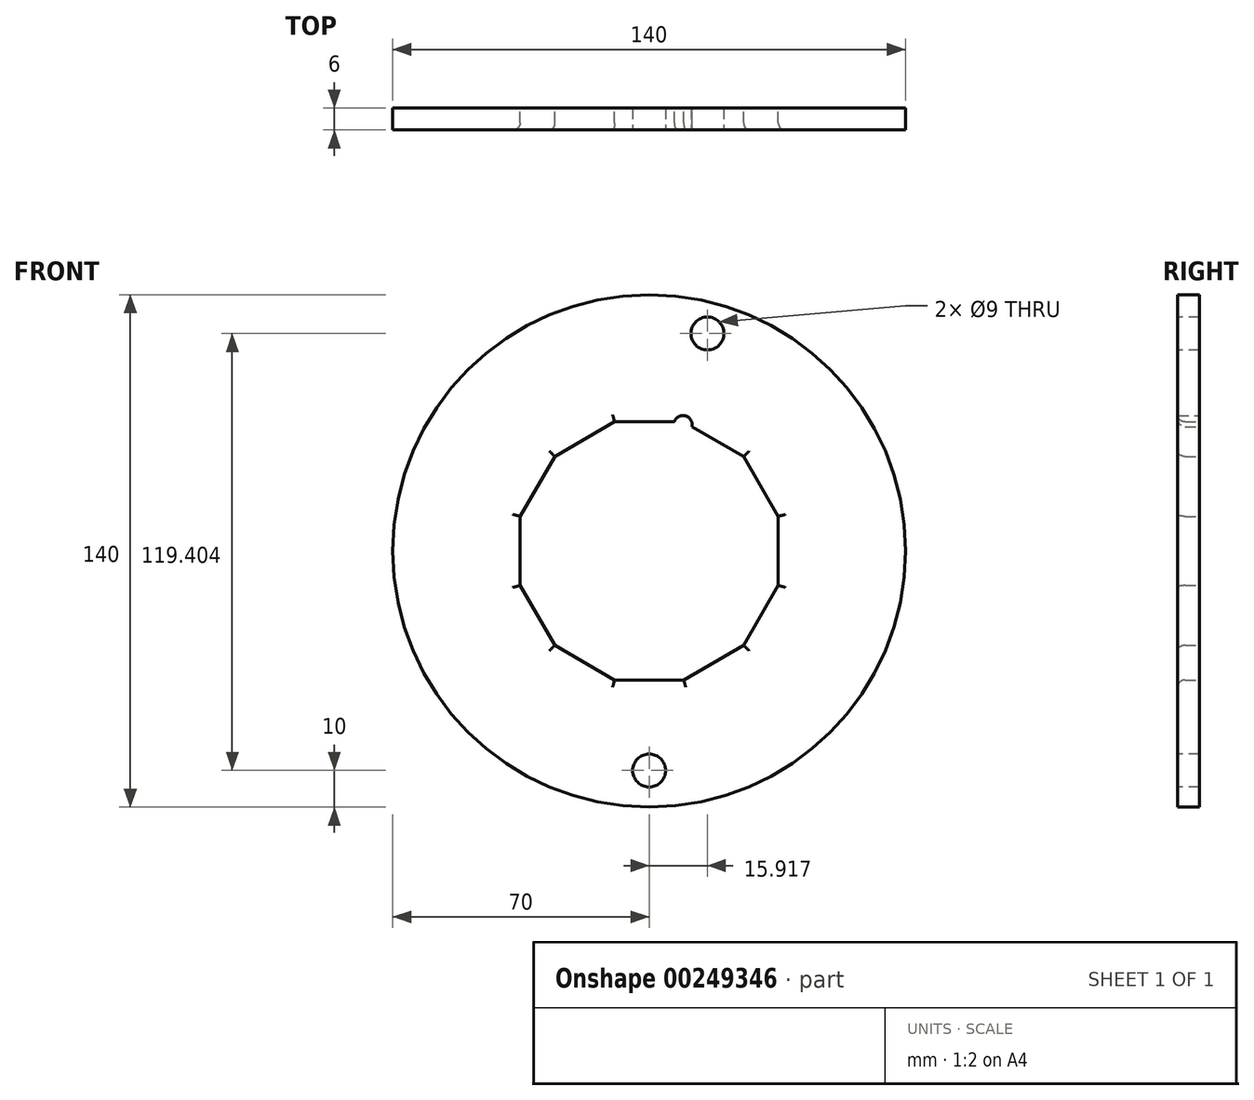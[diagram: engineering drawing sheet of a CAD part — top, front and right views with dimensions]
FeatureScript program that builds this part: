
annotation { "Feature Type Name" : "Feature", "Feature Type Description" : "" }
export const myFeature = defineFeature(function(context is Context, id is Id, definition is map)
    precondition{}
    {
        {
            var Q0;
            Q0=qCreatedBy(makeId("Front.planeOp"),FACE);
            var sketch = newSketch(context, id + "F0", { "sketchPlane" : qUnion([Q0])});
            skCircle(sketch, "E0.cCircle", {"center": v(0, 0) * mm, "radius": 35.25 * mm, "construction": true});
            skLineSegment(sketch, "E0.0", {"start": v(-9.45, 35.25) * mm, "end": v(9.45, 35.25) * mm});
            skLineSegment(sketch, "E0.1", {"start": v(9.45, 35.25) * mm, "end": v(25.8, 25.8) * mm});
            skLineSegment(sketch, "E0.2", {"start": v(25.8, 25.8) * mm, "end": v(35.25, 9.45) * mm});
            skLineSegment(sketch, "E0.3", {"start": v(35.25, 9.45) * mm, "end": v(35.25, -9.45) * mm});
            skLineSegment(sketch, "E0.4", {"start": v(35.25, -9.45) * mm, "end": v(25.8, -25.8) * mm});
            skLineSegment(sketch, "E0.5", {"start": v(25.8, -25.8) * mm, "end": v(9.45, -35.25) * mm});
            skLineSegment(sketch, "E0.6", {"start": v(9.45, -35.25) * mm, "end": v(-9.45, -35.25) * mm});
            skLineSegment(sketch, "E0.7", {"start": v(-9.45, -35.25) * mm, "end": v(-25.8, -25.8) * mm});
            skLineSegment(sketch, "E0.8", {"start": v(-25.8, -25.8) * mm, "end": v(-35.25, -9.45) * mm});
            skLineSegment(sketch, "E0.9", {"start": v(-35.25, -9.45) * mm, "end": v(-35.25, 9.45) * mm});
            skLineSegment(sketch, "E0.10", {"start": v(-35.25, 9.45) * mm, "end": v(-25.8, 25.8) * mm});
            skLineSegment(sketch, "E0.11", {"start": v(-25.8, 25.8) * mm, "end": v(-9.45, 35.25) * mm});
            skPoint(sketch, "E0.0.midPoint", {"position": v(0, 35.25) * mm});
            skCircle(sketch, "E1", {"center": v(0, 0) * mm, "radius": 70 * mm});
            skSolve(sketch);
        }
        {
            var Q0;
            Q0=makeQuery(id+"F0.imprint","IMPRINT",FACE,{"disambiguationData":[TD([[makeQuery(id+"F0.imprint","IMPRINT",EDGE,{"derivedFrom":sQuery(id+"F0.wireOp",EDGE,"E0.0")}),1.0]])]});
            extrude(context, id + "F1", {"entities" : qUnion([Q0]), "depth" : 6 * mm, "symmetric" : true});
        }
        {
            var Q0;
            Q0=qCreatedBy(makeId("Front.planeOp"),FACE);
            var sketch = newSketch(context, id + "F2", { "sketchPlane" : qUnion([Q0])});
            skCircle(sketch, "E2", {"center": v(9.24, 34.48) * mm, "radius": 2.5 * mm});
            skLineSegment(sketch, "E3", {"start": v(9.24, 34.48) * mm, "end": v(0, 0) * mm, "construction": true});
            skSolve(sketch);
        }
        {
            var Q0;
            Q0=makeQuery(id+"F1.opExtrude","CAP_EDGE",EDGE,{"disambiguationData":[OSD([sQuery(id+"F0.wireOp",EDGE,"E0.11")])],"isStart":false});
            var Q1;
            Q1=makeQuery(id+"F1.opExtrude","CAP_EDGE",EDGE,{"disambiguationData":[OSD([sQuery(id+"F0.wireOp",EDGE,"E0.0")])],"isStart":false});
            var Q2;
            Q2=makeQuery(id+"F1.opExtrude","CAP_EDGE",EDGE,{"disambiguationData":[OSD([sQuery(id+"F0.wireOp",EDGE,"E0.1")])],"isStart":false});
            var Q3;
            Q3=makeQuery(id+"F1.opExtrude","CAP_EDGE",EDGE,{"disambiguationData":[OSD([sQuery(id+"F0.wireOp",EDGE,"E0.2")])],"isStart":false});
            var Q4;
            Q4=makeQuery(id+"F1.opExtrude","CAP_EDGE",EDGE,{"disambiguationData":[OSD([sQuery(id+"F0.wireOp",EDGE,"E0.3")])],"isStart":false});
            var Q5;
            Q5=makeQuery(id+"F1.opExtrude","CAP_EDGE",EDGE,{"disambiguationData":[OSD([sQuery(id+"F0.wireOp",EDGE,"E0.4")])],"isStart":false});
            var Q6;
            Q6=makeQuery(id+"F1.opExtrude","CAP_EDGE",EDGE,{"disambiguationData":[OSD([sQuery(id+"F0.wireOp",EDGE,"E0.5")])],"isStart":false});
            var Q7;
            Q7=makeQuery(id+"F1.opExtrude","CAP_EDGE",EDGE,{"disambiguationData":[OSD([sQuery(id+"F0.wireOp",EDGE,"E0.6")])],"isStart":false});
            var Q8;
            Q8=makeQuery(id+"F1.opExtrude","CAP_EDGE",EDGE,{"disambiguationData":[OSD([sQuery(id+"F0.wireOp",EDGE,"E0.7")])],"isStart":false});
            var Q9;
            Q9=makeQuery(id+"F1.opExtrude","CAP_EDGE",EDGE,{"disambiguationData":[OSD([sQuery(id+"F0.wireOp",EDGE,"E0.8")])],"isStart":false});
            var Q10;
            Q10=makeQuery(id+"F1.opExtrude","CAP_EDGE",EDGE,{"disambiguationData":[OSD([sQuery(id+"F0.wireOp",EDGE,"E0.9")])],"isStart":false});
            var Q11;
            Q11=makeQuery(id+"F1.opExtrude","CAP_EDGE",EDGE,{"disambiguationData":[OSD([sQuery(id+"F0.wireOp",EDGE,"E0.10")])],"isStart":false});
            fillet(context, id + "F3", {"entities" : qUnion([Q0, Q1, Q2, Q3, Q4, Q5, Q6, Q7, Q8, Q9, Q10, Q11]), "radius" : 2 * mm, "tangentPropagation" : true, "allowEdgeOverflow" : false});
        }
        {
            var Q0;
            Q0=makeQuery(id+"F2.imprint","IMPRINT",FACE,{"disambiguationData":[TD([[makeQuery(id+"F2.imprint","IMPRINT",EDGE,{"derivedFrom":sQuery(id+"F2.wireOp",EDGE,"E2")}),1.0]])]});
            extrude(context, id + "F4", {"entities" : qUnion([Q0]), "operationType" : NewBodyOperationType.REMOVE, "offsetDistance" : 25 * mm, "depth" : 25 * mm, "symmetric" : true});
        }
        {
            var Q0;
            Q0=qCreatedBy(makeId("Front.planeOp"),FACE);
            var sketch = newSketch(context, id + "F5", { "sketchPlane" : qUnion([Q0])});
            skCircle(sketch, "E4", {"center": v(0, -60) * mm, "radius": 4.5 * mm});
            skSolve(sketch);
        }
        {
            var Q0;
            Q0=qSketchRegion(id+"F5",true);
            extrude(context, id + "F6", {"entities" : qUnion([Q0]), "operationType" : NewBodyOperationType.REMOVE, "oppositeDirection" : true, "depth" : 25 * mm, "symmetric" : true});
        }
        {
            var Q0;
            Q0=qCreatedBy(makeId("Front.planeOp"),FACE);
            var sketch = newSketch(context, id + "F7", { "sketchPlane" : qUnion([Q0])});
            skLineSegment(sketch, "E5", {"start": v(0, 0) * mm, "end": v(15.92, 59.4) * mm, "construction": true});
            skCircle(sketch, "E6", {"center": v(15.92, 59.4) * mm, "radius": 4.5 * mm});
            skSolve(sketch);
        }
        {
            var Q0;
            Q0=qSketchRegion(id+"F7",true);
            extrude(context, id + "F8", {"entities" : qUnion([Q0]), "operationType" : NewBodyOperationType.REMOVE, "oppositeDirection" : true, "depth" : 25 * mm, "symmetric" : true});
        }
    });
